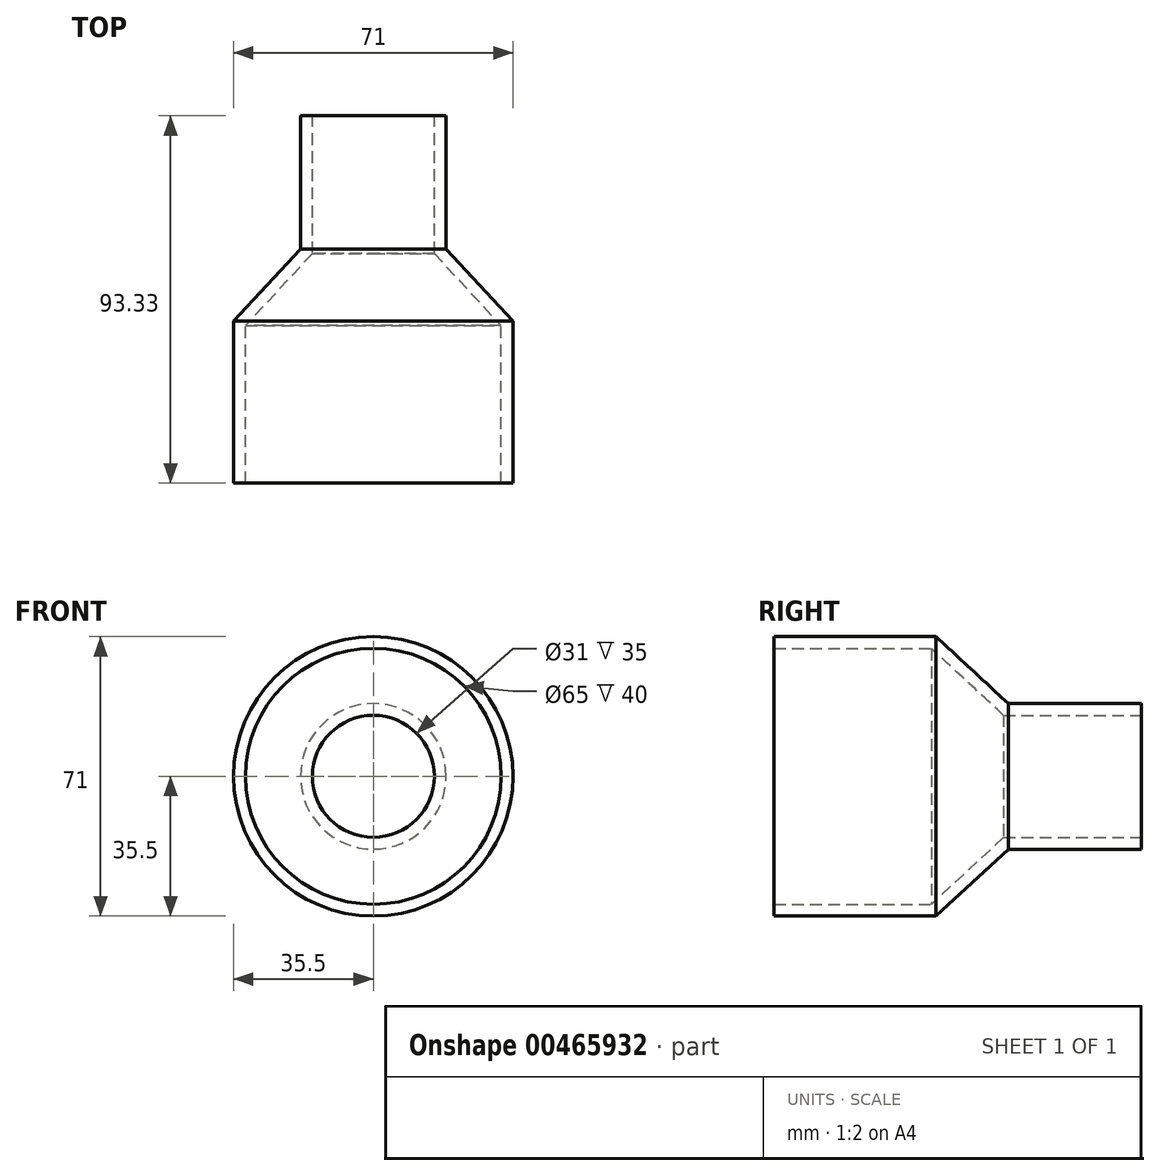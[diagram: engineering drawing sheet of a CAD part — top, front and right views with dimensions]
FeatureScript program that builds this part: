
annotation { "Feature Type Name" : "Feature", "Feature Type Description" : "" }
export const myFeature = defineFeature(function(context is Context, id is Id, definition is map)
    precondition{}
    {
        {
            var Q0;
            Q0=qCreatedBy(makeId("Top.planeOp"),FACE);
            var sketch = newSketch(context, id + "F0", { "sketchPlane" : qUnion([Q0])});
            skLineSegment(sketch, "E0", {"start": v(-15.5, 53.33) * mm, "end": v(-20.52, 53.33) * mm});
            skLineSegment(sketch, "E1", {"start": v(-32.5, -40) * mm, "end": v(-35.5, -40) * mm});
            skPoint(sketch, "E2.orphan", {"position": v(0, -40) * mm});
            skPoint(sketch, "E3.orphan", {"position": v(0, 53.33) * mm});
            skLineSegment(sketch, "E4", {"start": v(0, 53.33) * mm, "end": v(0, -40) * mm, "construction": true});
            skLineSegment(sketch, "E5", {"start": v(-15.5, 53.33) * mm, "end": v(-15.5, 18.33) * mm});
            skLineSegment(sketch, "E6", {"start": v(-32.5, -40) * mm, "end": v(-32.5, 0) * mm});
            skLineSegment(sketch, "E7", {"start": v(-15.5, 18.33) * mm, "end": v(-32.5, 0) * mm});
            skLineSegment(sketch, "E8.0", {"start": v(-35.5, -40) * mm, "end": v(-35.5, 1.18) * mm});
            skLineSegment(sketch, "E8.1", {"start": v(-18.5, 19.5) * mm, "end": v(-35.5, 1.18) * mm});
            skLineSegment(sketch, "E8.2", {"start": v(-18.5, 53.33) * mm, "end": v(-18.5, 19.5) * mm});
            skSolve(sketch);
        }
        {
            var Q0;
            Q0=makeQuery(id+"F0.imprint","IMPRINT",FACE,{"disambiguationData":[TD([[makeQuery(id+"F0.imprint","IMPRINT",EDGE,{"derivedFrom":sQuery(id+"F0.wireOp",EDGE,"E1")}),-1.0]])]});
            var Q1;
            Q1=sQuery(id+"F0.wireOp",EDGE,"E4");
            revolve(context, id + "F1", {"entities" : qUnion([Q0]), "axis" : qUnion([Q1]), "revolveType" : RevolveType.FULL});
        }
    });
